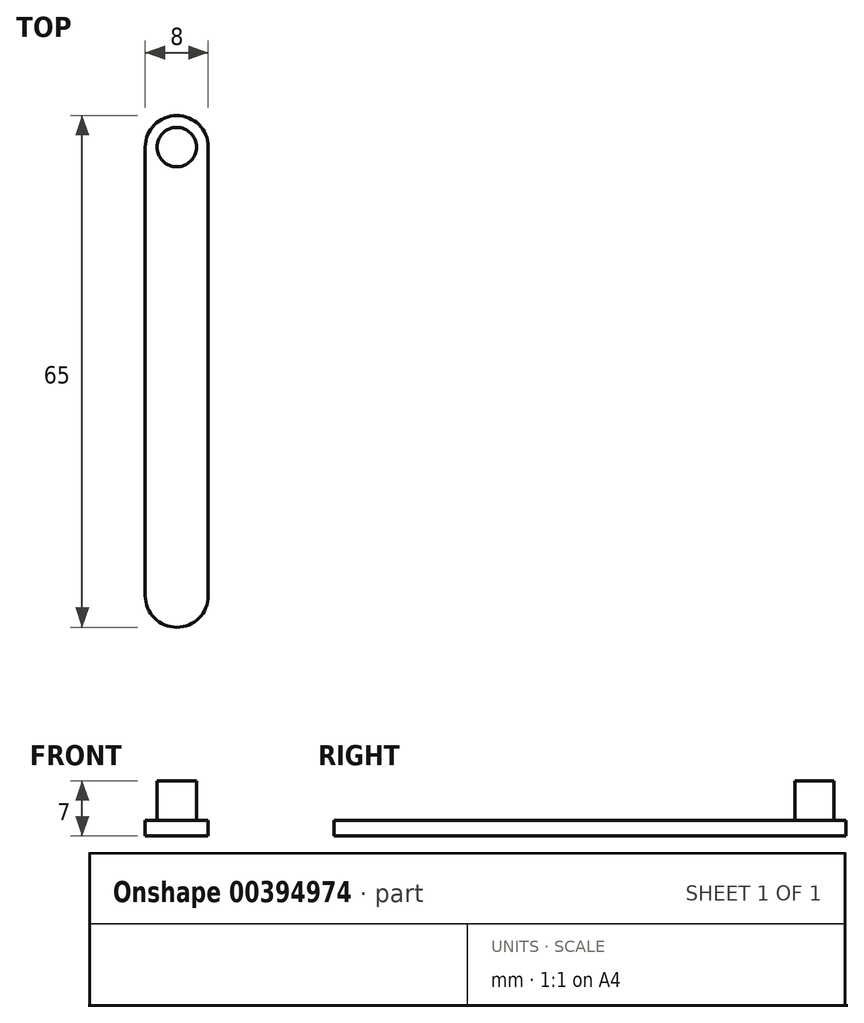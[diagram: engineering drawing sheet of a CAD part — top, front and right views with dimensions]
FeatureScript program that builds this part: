
annotation { "Feature Type Name" : "Feature", "Feature Type Description" : "" }
export const myFeature = defineFeature(function(context is Context, id is Id, definition is map)
    precondition{}
    {
        {
            var Q0;
            Q0=qCreatedBy(makeId("Top.planeOp"),FACE);
            cPlane(context, id + "F0", {"entities" : qUnion([Q0]), "cplaneType" : CPlaneType.OFFSET, "offset" : 0 * mm, "width" : 150 * mm, "height" : 150 * mm});
        }
        {
            var Q0;
            Q0=qCreatedBy(id+"F0.planeOp",FACE);
            var sketch = newSketch(context, id + "F1", { "sketchPlane" : qUnion([Q0])});
            skLineSegment(sketch, "E0.bottom", {"start": v(-11.07, 17.2) * mm, "end": v(-11.07, 17.2) * mm});
            skLineSegment(sketch, "E0.top", {"start": v(-11.07, -47.8) * mm, "end": v(-11.07, -47.8) * mm});
            skLineSegment(sketch, "E0.left", {"start": v(-15.07, 13.2) * mm, "end": v(-15.07, -43.8) * mm});
            skLineSegment(sketch, "E0.right", {"start": v(-7.07, 13.2) * mm, "end": v(-7.07, -43.8) * mm});
            skCircle(sketch, "E1", {"center": v(-11.07, 13.2) * mm, "radius": 2.5 * mm});
            skPoint(sketch, "E1.centerSnap0", {"position": v(-11.07, 17.2) * mm});
            skPoint(sketch, "E2.visualSharp", {"position": v(-15.07, 17.2) * mm});
            skArc(sketch, "E2.filletArc", {"start": v(-11.07, 17.2) * mm, "mid": v(-13.9, 16.04) * mm, "end": v(-15.07, 13.2) * mm});
            skPoint(sketch, "E3.visualSharp", {"position": v(-7.07, 17.2) * mm});
            skArc(sketch, "E3.filletArc", {"start": v(-7.07, 13.2) * mm, "mid": v(-8.24, 16.04) * mm, "end": v(-11.07, 17.2) * mm});
            skPoint(sketch, "E4.visualSharp", {"position": v(-15.07, -47.8) * mm});
            skArc(sketch, "E4.filletArc", {"start": v(-15.07, -43.8) * mm, "mid": v(-13.9, -46.62) * mm, "end": v(-11.07, -47.8) * mm});
            skPoint(sketch, "E5.visualSharp", {"position": v(-7.07, -47.8) * mm});
            skArc(sketch, "E5.filletArc", {"start": v(-11.07, -47.8) * mm, "mid": v(-8.24, -46.62) * mm, "end": v(-7.07, -43.8) * mm});
            skSolve(sketch);
        }
        {
            var Q0;
            Q0=makeQuery(id+"F1.imprint","IMPRINT",FACE,{"disambiguationData":[TD([[makeQuery(id+"F1.imprint","IMPRINT",EDGE,{"derivedFrom":sQuery(id+"F1.wireOp",EDGE,"E1")}),1.0]])]});
            extrude(context, id + "F2", {"entities" : qUnion([Q0]), "depth" : 7 * mm});
        }
        {
            var Q0;
            Q0=makeQuery(id+"F1.imprint","IMPRINT",FACE,{"disambiguationData":[TD([[makeQuery(id+"F1.imprint","IMPRINT",EDGE,{"derivedFrom":sQuery(id+"F1.wireOp",EDGE,"E0.left")}),1.0]])]});
            extrude(context, id + "F3", {"entities" : qUnion([Q0]), "operationType" : NewBodyOperationType.ADD, "depth" : 2 * mm});
        }
    });
